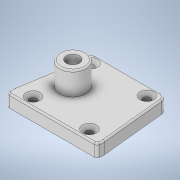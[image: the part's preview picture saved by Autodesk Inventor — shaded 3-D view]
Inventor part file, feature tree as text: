
AUTODESK INVENTOR PART (.ipt)
format: ipt  version: 2020.3 (Build 243373000, 373)  size: 356,352 bytes
history: native  units: mm
features: sketch x3, extrude x3, hole x3, fillet x2
ambient origin geometry x8: Origin, YZ Plane, XZ Plane, XY Plane, X Axis, Y Axis, Z Axis, Center Point
bodies: Body1 (feature_tree)
feature tree (11):
  sketch  "Sketch1"  dims[d0=135.0deg d4=24.6mm]
  extrude  "Extrusion12"  Depth=24.6mm
  extrude  "Extrusion13"  Depth=70.0mm
  extrude  "Extrusion14"  Depth=6.5mm
  hole  "Hole3"  [1 undecoded]
  fillet  "Fillet10"  Radius=6.0mm
  fillet  "Fillet11"  Radius=2.0mm
  hole  "Hole4"  [1 undecoded]
  hole  "Hole5"  [1 undecoded]
  sketch  "Sketch2"  dims[d5=12.4mm d6=70.0mm]
  sketch  "Sketch4"  dims[d7=60.0mm d9=8.5mm d10=135.0deg d12=6.0mm d13=2.0mm d14=2.0mm d16=20.0mm d23=5.0mm d29=130.0mm d32=15.0mm d33=4.0mm d34=28.4mm d38=4.0mm d40=6.8mm d49=30.0mm d50=84.0mm d51=3.0mm d52=3.0mm d53=1.5mm d54=20.0mm d59=1.0mm d60=90.0mm d61=135.0deg d70=135.0deg d82=0.7mm d83=0.7mm d84=0.7mm d85=0.7mm d86=6.0mm d102=18.0mm d103=4.0mm d104=0.0mm d105=4.0mm d106=0.0mm d107=11.4mm d108=0.0mm d116=4.2mm d117=6.0mm d118=5.6mm d119=0.85mm d120=90.0deg d121=4.2mm d122=0.0mm d123=2.0mm d125=0.5mm d126=2.0mm d128=1.0mm d135=2.3mm d136=6.0mm d137=4.5mm d138=2.0mm d139=90.0deg d140=6.5mm d141=0.0mm d142=5.6mm d143=6.0mm d144=9.0mm d145=1.0mm d146=90.0deg d147=6.5mm d148=0.0mm]
note: 3 required parameter values undecoded (feature->parameter linkage not recoverable at this tier; creation-order binding heuristic only, values carry confidence <= 0.55)
